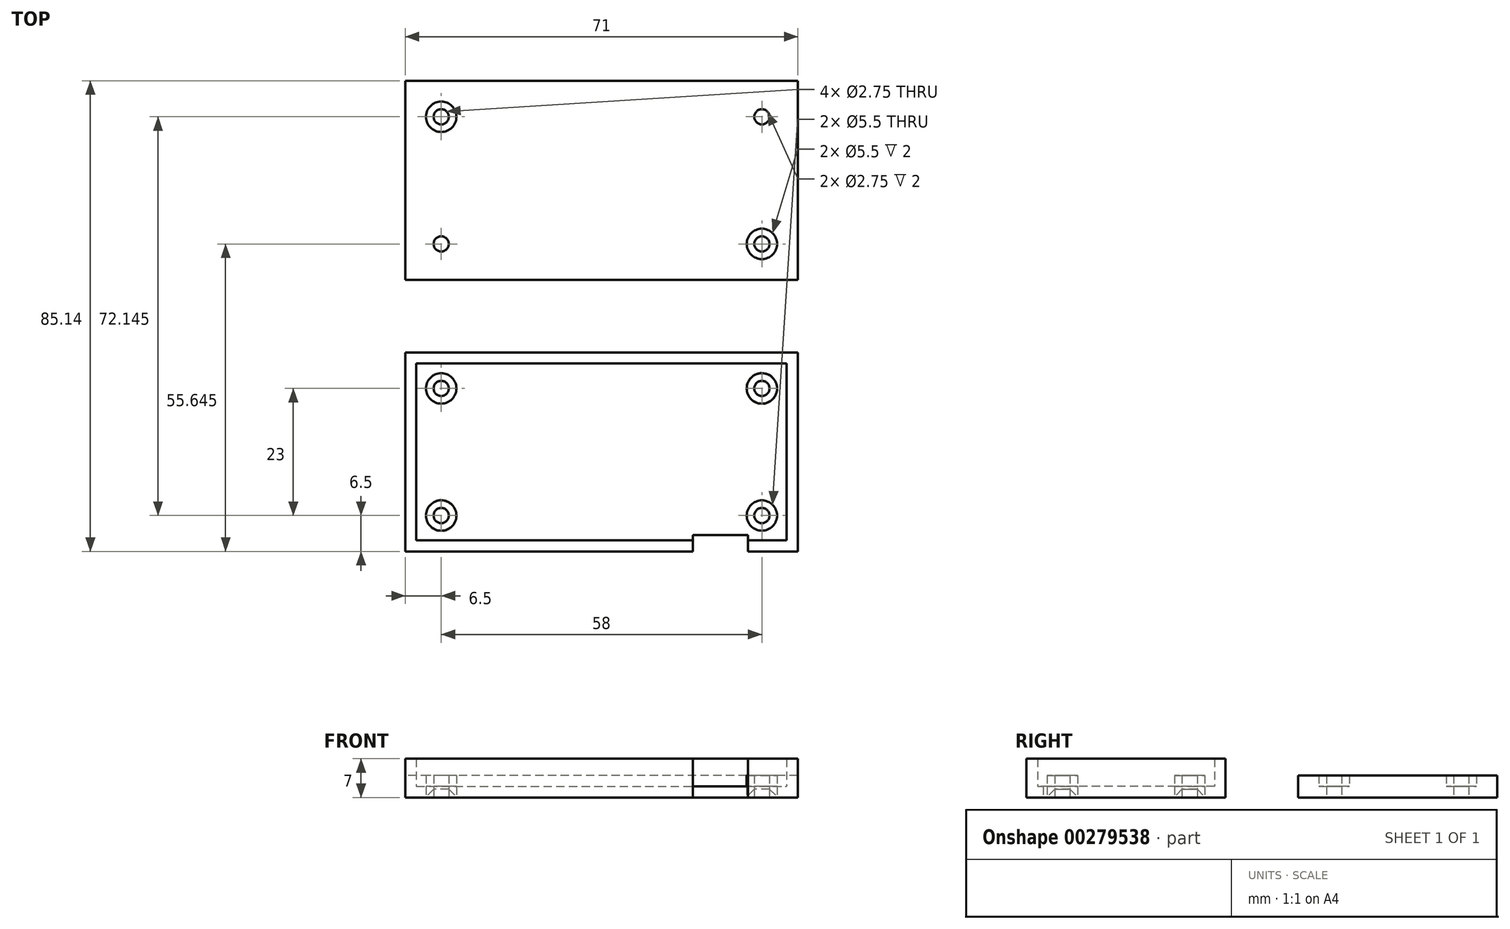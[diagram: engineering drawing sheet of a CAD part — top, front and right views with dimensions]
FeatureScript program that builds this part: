
annotation { "Feature Type Name" : "Feature", "Feature Type Description" : "" }
export const myFeature = defineFeature(function(context is Context, id is Id, definition is map)
    precondition{}
    {
        {
            var Q0;
            Q0=qCreatedBy(makeId("Top.planeOp"),FACE);
            var sketch = newSketch(context, id + "F0", { "sketchPlane" : qUnion([Q0])});
            skLineSegment(sketch, "E0.bottom", {"start": v(32.5, -15) * mm, "end": v(-32.5, -15) * mm});
            skLineSegment(sketch, "E0.top", {"start": v(32.5, 15) * mm, "end": v(-32.5, 15) * mm});
            skLineSegment(sketch, "E0.left", {"start": v(32.5, -15) * mm, "end": v(32.5, 15) * mm});
            skLineSegment(sketch, "E0.right", {"start": v(-32.5, -15) * mm, "end": v(-32.5, 15) * mm});
            skPoint(sketch, "E0.middle", {"position": v(0, 0) * mm});
            skCircle(sketch, "E1", {"center": v(29, 11.5) * mm, "radius": 1.38 * mm});
            skLineSegment(sketch, "E2", {"start": v(29, 15) * mm, "end": v(29, 11.5) * mm, "construction": true});
            skLineSegment(sketch, "E3", {"start": v(29, 11.5) * mm, "end": v(32.5, 11.5) * mm, "construction": true});
            skCircle(sketch, "E4.MirrorC", {"center": v(29, -11.5) * mm, "radius": 1.38 * mm});
            skCircle(sketch, "E5.MirrorC", {"center": v(-29, -11.5) * mm, "radius": 1.38 * mm});
            skCircle(sketch, "E6.MirrorC", {"center": v(-29, 11.5) * mm, "radius": 1.38 * mm});
            skLineSegment(sketch, "E7.0", {"start": v(33.5, 16) * mm, "end": v(-33.5, 16) * mm});
            skLineSegment(sketch, "E7.1", {"start": v(33.5, -16) * mm, "end": v(33.5, 16) * mm});
            skLineSegment(sketch, "E7.2", {"start": v(33.5, -16) * mm, "end": v(-33.5, -16) * mm});
            skLineSegment(sketch, "E7.3", {"start": v(-33.5, -16) * mm, "end": v(-33.5, 16) * mm});
            skLineSegment(sketch, "E8.0", {"start": v(35.5, 18) * mm, "end": v(-35.5, 18) * mm});
            skLineSegment(sketch, "E8.1", {"start": v(35.5, -18) * mm, "end": v(35.5, 18) * mm});
            skLineSegment(sketch, "E8.2", {"start": v(35.5, -18) * mm, "end": v(-35.5, -18) * mm});
            skLineSegment(sketch, "E8.3", {"start": v(-35.5, -18) * mm, "end": v(-35.5, 18) * mm});
            skLineSegment(sketch, "E9", {"start": v(-32.5, -15) * mm, "end": v(21.5, -15) * mm, "construction": true});
            skLineSegment(sketch, "E10.bottom", {"start": v(26.5, -18) * mm, "end": v(16.5, -18) * mm});
            skLineSegment(sketch, "E10.top", {"start": v(26.5, -15) * mm, "end": v(16.5, -15) * mm});
            skLineSegment(sketch, "E10.left", {"start": v(26.5, -18) * mm, "end": v(26.5, -15) * mm});
            skLineSegment(sketch, "E10.right", {"start": v(16.5, -18) * mm, "end": v(16.5, -15) * mm});
            skPoint(sketch, "E10.middle", {"position": v(21.5, -16.5) * mm});
            skCircle(sketch, "E11", {"center": v(29, 11.5) * mm, "radius": 2.75 * mm});
            skCircle(sketch, "E12.MirrorC", {"center": v(29, -11.5) * mm, "radius": 2.75 * mm});
            skCircle(sketch, "E13.MirrorC", {"center": v(-29, -11.5) * mm, "radius": 2.75 * mm});
            skCircle(sketch, "E14.MirrorC", {"center": v(-29, 11.5) * mm, "radius": 2.75 * mm});
            skSolve(sketch);
        }
        {
            var Q0;
            Q0=makeQuery(id+"F0.imprint","IMPRINT",FACE,{"disambiguationData":[TD([[makeQuery(id+"F0.imprint","IMPRINT",EDGE,{"derivedFrom":sQuery(id+"F0.wireOp",EDGE,"E7.0")}),-1.0]])]});
            var Q1;
            Q1=makeQuery(id+"F0.imprint","IMPRINT",FACE,{"disambiguationData":[TD([[makeQuery(id+"F0.imprint","IMPRINT",EDGE,{"derivedFrom":sQuery(id+"F0.wireOp",EDGE,"E0.top")}),1.0]])]});
            var Q2;
            Q2=makeQuery(id+"F0.imprint","IMPRINT",FACE,{"disambiguationData":[TD([[makeQuery(id+"F0.imprint","IMPRINT",EDGE,{"derivedFrom":sQuery(id+"F0.wireOp",EDGE,"E0.top")}),-1.0]])]});
            var Q3;
            {var subQ5=sQuery(id+"F0.wireOp",EDGE,"E10.top");Q3=makeQuery(id+"F0.imprint","IMPRINT",FACE,{"disambiguationData":[TD([[makeQuery(id+"F0.imprint","IMPRINT",EDGE,{"derivedFrom":subQ5}),1.0]])]});}
            var Q4;
            Q4=makeQuery(id+"F0.imprint","IMPRINT",FACE,{"disambiguationData":[TD([[makeQuery(id+"F0.imprint","IMPRINT",EDGE,{"derivedFrom":sQuery(id+"F0.wireOp",EDGE,"E1")}),-1.0]])]});
            var Q5;
            Q5=makeQuery(id+"F0.imprint","IMPRINT",FACE,{"disambiguationData":[TD([[makeQuery(id+"F0.imprint","IMPRINT",EDGE,{"derivedFrom":sQuery(id+"F0.wireOp",EDGE,"E4.MirrorC")}),1.0]])]});
            var Q6;
            Q6=makeQuery(id+"F0.imprint","IMPRINT",FACE,{"disambiguationData":[TD([[makeQuery(id+"F0.imprint","IMPRINT",EDGE,{"derivedFrom":sQuery(id+"F0.wireOp",EDGE,"E6.MirrorC")}),1.0]])]});
            var Q7;
            Q7=makeQuery(id+"F0.imprint","IMPRINT",FACE,{"disambiguationData":[TD([[makeQuery(id+"F0.imprint","IMPRINT",EDGE,{"derivedFrom":sQuery(id+"F0.wireOp",EDGE,"E5.MirrorC")}),-1.0]])]});
            var Q8;
            {var subQ5=sQuery(id+"F0.wireOp",EDGE,"E10.bottom");Q8=makeQuery(id+"F0.imprint","IMPRINT",FACE,{"disambiguationData":[TD([[makeQuery(id+"F0.imprint","IMPRINT",EDGE,{"derivedFrom":subQ5}),-1.0]])]});}
            extrude(context, id + "F1", {"entities" : qUnion([Q0, Q1, Q2, Q3, Q4, Q5, Q6, Q7, Q8]), "depth" : 2 * mm});
        }
        {
            var Q0;
            Q0=makeQuery(id+"F0.imprint","IMPRINT",FACE,{"disambiguationData":[TD([[makeQuery(id+"F0.imprint","IMPRINT",EDGE,{"derivedFrom":sQuery(id+"F0.wireOp",EDGE,"E1")}),-1.0]])]});
            var Q1;
            Q1=makeQuery(id+"F0.imprint","IMPRINT",FACE,{"disambiguationData":[TD([[makeQuery(id+"F0.imprint","IMPRINT",EDGE,{"derivedFrom":sQuery(id+"F0.wireOp",EDGE,"E4.MirrorC")}),1.0]])]});
            var Q2;
            Q2=makeQuery(id+"F0.imprint","IMPRINT",FACE,{"disambiguationData":[TD([[makeQuery(id+"F0.imprint","IMPRINT",EDGE,{"derivedFrom":sQuery(id+"F0.wireOp",EDGE,"E6.MirrorC")}),1.0]])]});
            var Q3;
            Q3=makeQuery(id+"F0.imprint","IMPRINT",FACE,{"disambiguationData":[TD([[makeQuery(id+"F0.imprint","IMPRINT",EDGE,{"derivedFrom":sQuery(id+"F0.wireOp",EDGE,"E5.MirrorC")}),-1.0]])]});
            extrude(context, id + "F2", {"entities" : qUnion([Q0, Q1, Q2, Q3]), "operationType" : NewBodyOperationType.ADD, "depth" : 4 * mm});
        }
        {
            var Q0;
            Q0=makeQuery(id+"F0.imprint","IMPRINT",FACE,{"disambiguationData":[TD([[makeQuery(id+"F0.imprint","IMPRINT",EDGE,{"derivedFrom":sQuery(id+"F0.wireOp",EDGE,"E7.0")}),-1.0]])]});
            extrude(context, id + "F3", {"entities" : qUnion([Q0]), "operationType" : NewBodyOperationType.ADD, "depth" : 7 * mm});
        }
        {
            var Q0;
            Q0=makeQuery(id+"F1.opExtrude","CAP_EDGE",EDGE,{"disambiguationData":[OSD([sQuery(id+"F0.wireOp",EDGE,"E5.MirrorC")])],"isStart":true});
            var Q1;
            Q1=makeQuery(id+"F1.opExtrude","CAP_EDGE",EDGE,{"disambiguationData":[OSD([sQuery(id+"F0.wireOp",EDGE,"E4.MirrorC")])],"isStart":true});
            var Q2;
            Q2=makeQuery(id+"F1.opExtrude","CAP_EDGE",EDGE,{"disambiguationData":[OSD([sQuery(id+"F0.wireOp",EDGE,"E1")])],"isStart":true});
            var Q3;
            Q3=makeQuery(id+"F1.opExtrude","CAP_EDGE",EDGE,{"disambiguationData":[OSD([sQuery(id+"F0.wireOp",EDGE,"E6.MirrorC")])],"isStart":true});
            chamfer(context, id + "F4", {"entities" : qUnion([Q0, Q1, Q2, Q3]), "width" : 1.5 * mm, "tangentPropagation" : true});
        }
        {
            var Q0;
            Q0=qCreatedBy(makeId("Top.planeOp"),FACE);
            var sketch = newSketch(context, id + "F5", { "sketchPlane" : qUnion([Q0])});
            skLineSegment(sketch, "E15.bottom", {"start": v(35.5, 31.14) * mm, "end": v(-35.5, 31.14) * mm});
            skLineSegment(sketch, "E15.top", {"start": v(35.5, 67.14) * mm, "end": v(-35.5, 67.14) * mm});
            skLineSegment(sketch, "E15.left", {"start": v(35.5, 31.14) * mm, "end": v(35.5, 67.14) * mm});
            skLineSegment(sketch, "E15.right", {"start": v(-35.5, 31.14) * mm, "end": v(-35.5, 67.14) * mm});
            skPoint(sketch, "E15.middle", {"position": v(0, 49.14) * mm});
            skLineSegment(sketch, "E16", {"start": v(29, 67.14) * mm, "end": v(29, 60.64) * mm, "construction": true});
            skLineSegment(sketch, "E17", {"start": v(29, 60.64) * mm, "end": v(35.5, 60.64) * mm, "construction": true});
            skCircle(sketch, "E18", {"center": v(29, 60.64) * mm, "radius": 1.38 * mm});
            skCircle(sketch, "E19", {"center": v(29, 60.64) * mm, "radius": 2.75 * mm});
            skCircle(sketch, "E20.MirrorC", {"center": v(-29, 60.64) * mm, "radius": 2.75 * mm});
            skCircle(sketch, "E21.MirrorC", {"center": v(-29, 60.64) * mm, "radius": 1.38 * mm});
            skPoint(sketch, "E22.endSnap0", {"position": v(35.5, 49.14) * mm});
            skCircle(sketch, "E23.MirrorC", {"center": v(29, 37.64) * mm, "radius": 2.75 * mm});
            skCircle(sketch, "E24.MirrorC", {"center": v(29, 37.64) * mm, "radius": 1.38 * mm});
            skCircle(sketch, "E25.MirrorC", {"center": v(-29, 37.64) * mm, "radius": 1.38 * mm});
            skCircle(sketch, "E26.MirrorC", {"center": v(-29, 37.64) * mm, "radius": 2.75 * mm});
            skSolve(sketch);
        }
        {
            var Q0;
            Q0=makeQuery(id+"F5.imprint","IMPRINT",FACE,{"disambiguationData":[TD([[makeQuery(id+"F5.imprint","IMPRINT",EDGE,{"derivedFrom":sQuery(id+"F5.wireOp",EDGE,"E21.MirrorC")}),-1.0]])]});
            var Q1;
            Q1=makeQuery(id+"F5.imprint","IMPRINT",FACE,{"disambiguationData":[TD([[makeQuery(id+"F5.imprint","IMPRINT",EDGE,{"derivedFrom":sQuery(id+"F5.wireOp",EDGE,"E20.MirrorC")}),-1.0]])]});
            var Q2;
            Q2=makeQuery(id+"F5.imprint","IMPRINT",FACE,{"disambiguationData":[TD([[makeQuery(id+"F5.imprint","IMPRINT",EDGE,{"derivedFrom":sQuery(id+"F5.wireOp",EDGE,"E25.MirrorC")}),-1.0]])]});
            var Q3;
            Q3=makeQuery(id+"F5.imprint","IMPRINT",FACE,{"disambiguationData":[TD([[makeQuery(id+"F5.imprint","IMPRINT",EDGE,{"derivedFrom":sQuery(id+"F5.wireOp",EDGE,"E25.MirrorC")}),1.0]])]});
            var Q4;
            Q4=makeQuery(id+"F5.imprint","IMPRINT",FACE,{"disambiguationData":[TD([[makeQuery(id+"F5.imprint","IMPRINT",EDGE,{"derivedFrom":sQuery(id+"F5.wireOp",EDGE,"E18")}),1.0]])]});
            var Q5;
            Q5=makeQuery(id+"F5.imprint","IMPRINT",FACE,{"disambiguationData":[TD([[makeQuery(id+"F5.imprint","IMPRINT",EDGE,{"derivedFrom":sQuery(id+"F5.wireOp",EDGE,"E18")}),-1.0]])]});
            var Q6;
            Q6=makeQuery(id+"F5.imprint","IMPRINT",FACE,{"disambiguationData":[TD([[makeQuery(id+"F5.imprint","IMPRINT",EDGE,{"derivedFrom":sQuery(id+"F5.wireOp",EDGE,"E24.MirrorC")}),-1.0]])]});
            var Q7;
            Q7=makeQuery(id+"F5.imprint","IMPRINT",FACE,{"disambiguationData":[TD([[makeQuery(id+"F5.imprint","IMPRINT",EDGE,{"derivedFrom":sQuery(id+"F5.wireOp",EDGE,"E15.bottom")}),-1.0]])]});
            var Q8;
            Q8=makeQuery(id+"F5.imprint","IMPRINT",FACE,{"disambiguationData":[TD([[makeQuery(id+"F5.imprint","IMPRINT",EDGE,{"derivedFrom":sQuery(id+"F5.wireOp",EDGE,"E23.MirrorC")}),-1.0]])]});
            extrude(context, id + "F6", {"entities" : qUnion([Q0, Q1, Q2, Q3, Q4, Q5, Q6, Q7, Q8]), "depth" : 2 * mm});
        }
        {
            var Q0;
            Q0=makeQuery(id+"F5.imprint","IMPRINT",FACE,{"disambiguationData":[TD([[makeQuery(id+"F5.imprint","IMPRINT",EDGE,{"derivedFrom":sQuery(id+"F5.wireOp",EDGE,"E25.MirrorC")}),-1.0]])]});
            var Q1;
            Q1=makeQuery(id+"F5.imprint","IMPRINT",FACE,{"disambiguationData":[TD([[makeQuery(id+"F5.imprint","IMPRINT",EDGE,{"derivedFrom":sQuery(id+"F5.wireOp",EDGE,"E23.MirrorC")}),-1.0]])]});
            var Q2;
            Q2=makeQuery(id+"F5.imprint","IMPRINT",FACE,{"disambiguationData":[TD([[makeQuery(id+"F5.imprint","IMPRINT",EDGE,{"derivedFrom":sQuery(id+"F5.wireOp",EDGE,"E18")}),-1.0]])]});
            var Q3;
            Q3=makeQuery(id+"F5.imprint","IMPRINT",FACE,{"disambiguationData":[TD([[makeQuery(id+"F5.imprint","IMPRINT",EDGE,{"derivedFrom":sQuery(id+"F5.wireOp",EDGE,"E20.MirrorC")}),-1.0]])]});
            extrude(context, id + "F7", {"entities" : qUnion([Q0, Q1, Q2, Q3]), "operationType" : NewBodyOperationType.ADD, "depth" : 4 * mm});
        }
    });
